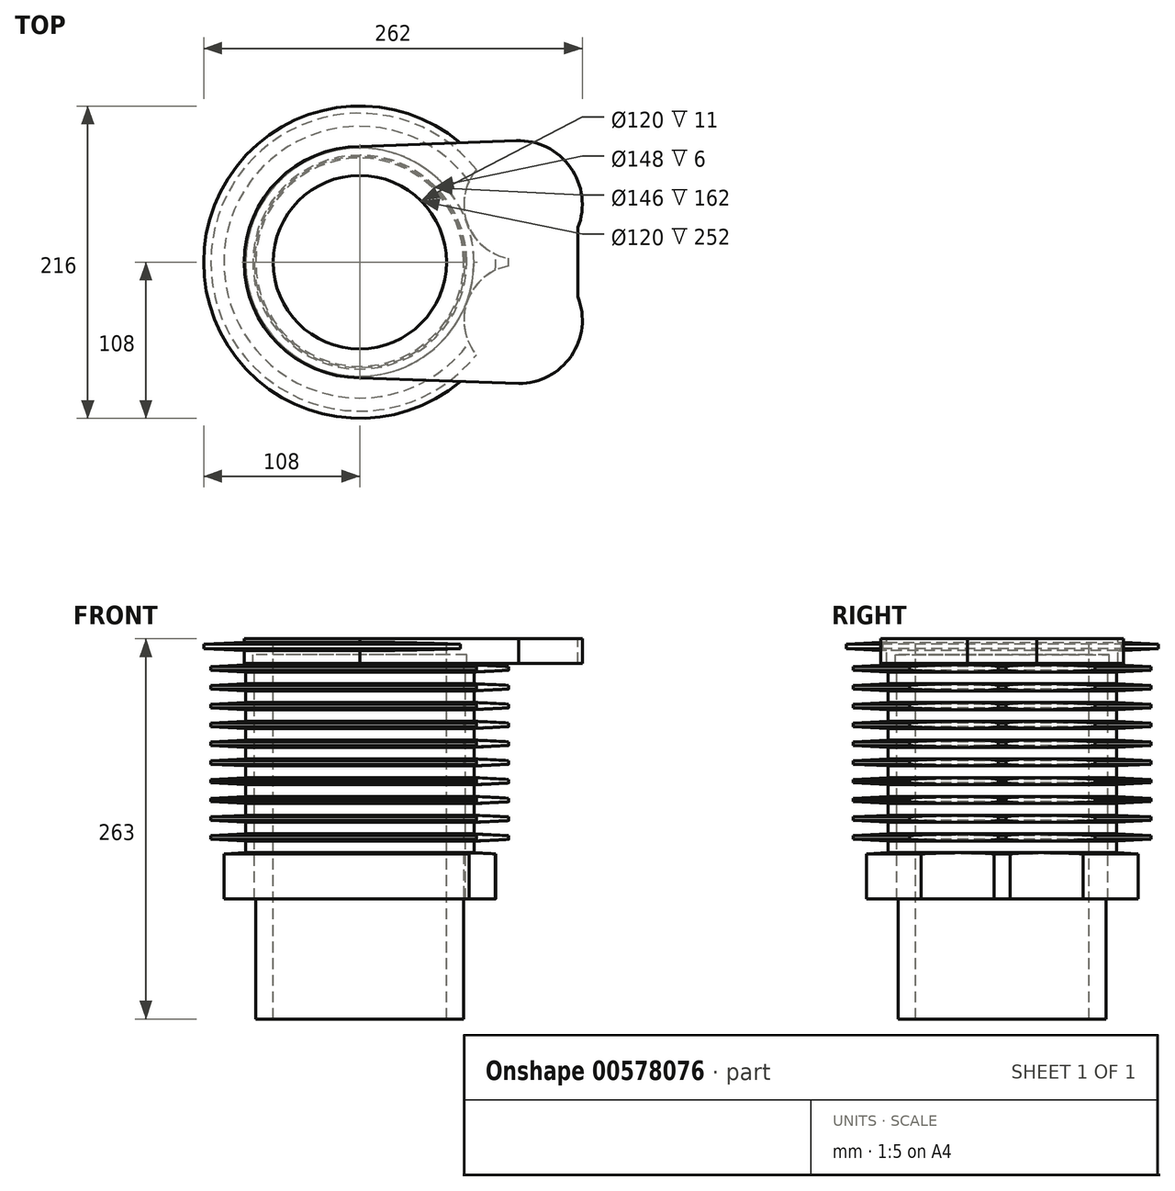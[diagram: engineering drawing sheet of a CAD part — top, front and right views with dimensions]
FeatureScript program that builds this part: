
annotation { "Feature Type Name" : "Feature", "Feature Type Description" : "" }
export const myFeature = defineFeature(function(context is Context, id is Id, definition is map)
    precondition{}
    {
        {
            var Q0;
            Q0=qCreatedBy(makeId("Front.planeOp"),FACE);
            var sketch = newSketch(context, id + "F0", { "sketchPlane" : qUnion([Q0])});
            skLineSegment(sketch, "E0", {"start": v(-60, 0) * mm, "end": v(-60, -252) * mm});
            skLineSegment(sketch, "E1", {"start": v(-60, 0) * mm, "end": v(-74, 0) * mm});
            skLineSegment(sketch, "E2", {"start": v(-65, 0) * mm, "end": v(-65, -179.28) * mm});
            skLineSegment(sketch, "E3", {"start": v(-74, 0) * mm, "end": v(-74, -7) * mm});
            skLineSegment(sketch, "E4", {"start": v(-74, -7) * mm, "end": v(-73, -7) * mm});
            skLineSegment(sketch, "E5", {"start": v(-73, -7) * mm, "end": v(-73, -169) * mm});
            skLineSegment(sketch, "E6", {"start": v(-73, -169) * mm, "end": v(-72, -169) * mm});
            skLineSegment(sketch, "E7", {"start": v(-72, -169) * mm, "end": v(-72, -252) * mm});
            skLineSegment(sketch, "E8", {"start": v(-72, -252) * mm, "end": v(-60, -252) * mm});
            skLineSegment(sketch, "E9", {"start": v(0, 0) * mm, "end": v(0, -66.25) * mm});
            skSolve(sketch);
        }
        {
            var Q0;
            {var subQ3=sQuery(id+"F0.wireOp",EDGE,"E0");Q0=makeQuery(id+"F0.imprint","IMPRINT",FACE,{"disambiguationData":[TD([[makeQuery(id+"F0.imprint","IMPRINT",EDGE,{"derivedFrom":subQ3}),-1.0]])]});}
            var Q1;
            Q1=sQuery(id+"F0.wireOp",EDGE,"E9");
            revolve(context, id + "F1", {"entities" : qUnion([Q0]), "axis" : qUnion([Q1]), "revolveType" : RevolveType.FULL});
        }
        {
            var Q0;
            Q0=qCreatedBy(makeId("Front.planeOp"),FACE);
            var sketch = newSketch(context, id + "F2", { "sketchPlane" : qUnion([Q0])});
            skLineSegment(sketch, "E10.0", {"start": v(-73, -7) * mm, "end": v(-73, -169) * mm});
            skLineSegment(sketch, "E11", {"start": v(-103, -8.26) * mm, "end": v(-103, -10.76) * mm});
            skLineSegment(sketch, "E12.0", {"start": v(-79, -7) * mm, "end": v(-79, -169) * mm});
            skLineSegment(sketch, "E13", {"start": v(-73, -7) * mm, "end": v(-79, -7) * mm});
            skLineSegment(sketch, "E14", {"start": v(-79, -7) * mm, "end": v(-103, -8.26) * mm});
            skPoint(sketch, "E15.orphan", {"position": v(-103, -9.1) * mm});
            skLineSegment(sketch, "E16", {"start": v(-103, -10.76) * mm, "end": v(-79, -12.02) * mm});
            skLineSegment(sketch, "E17", {"start": v(-79, -169) * mm, "end": v(-73, -169) * mm});
            skLineSegment(sketch, "E18.0.1.0", {"start": v(-79, -20) * mm, "end": v(-103, -21.26) * mm});
            skLineSegment(sketch, "E18.0.1.1", {"start": v(-103, -23.76) * mm, "end": v(-79, -25.02) * mm});
            skLineSegment(sketch, "E18.0.1.2", {"start": v(-103, -21.26) * mm, "end": v(-103, -23.76) * mm});
            skLineSegment(sketch, "E18.0.2.0", {"start": v(-79, -33) * mm, "end": v(-103, -34.26) * mm});
            skLineSegment(sketch, "E18.0.2.1", {"start": v(-103, -36.76) * mm, "end": v(-79, -38.02) * mm});
            skLineSegment(sketch, "E18.0.2.2", {"start": v(-103, -34.26) * mm, "end": v(-103, -36.76) * mm});
            skLineSegment(sketch, "E18.0.3.0", {"start": v(-79, -46) * mm, "end": v(-103, -47.26) * mm});
            skLineSegment(sketch, "E18.0.3.1", {"start": v(-103, -49.76) * mm, "end": v(-79, -51.02) * mm});
            skLineSegment(sketch, "E18.0.3.2", {"start": v(-103, -47.26) * mm, "end": v(-103, -49.76) * mm});
            skLineSegment(sketch, "E18.0.4.0", {"start": v(-79, -59) * mm, "end": v(-103, -60.26) * mm});
            skLineSegment(sketch, "E18.0.4.1", {"start": v(-103, -62.76) * mm, "end": v(-79, -64.02) * mm});
            skLineSegment(sketch, "E18.0.4.2", {"start": v(-103, -60.26) * mm, "end": v(-103, -62.76) * mm});
            skLineSegment(sketch, "E18.0.5.0", {"start": v(-79, -72) * mm, "end": v(-103, -73.26) * mm});
            skLineSegment(sketch, "E18.0.5.1", {"start": v(-103, -75.76) * mm, "end": v(-79, -77.02) * mm});
            skLineSegment(sketch, "E18.0.5.2", {"start": v(-103, -73.26) * mm, "end": v(-103, -75.76) * mm});
            skLineSegment(sketch, "E18.0.6.0", {"start": v(-79, -85) * mm, "end": v(-103, -86.26) * mm});
            skLineSegment(sketch, "E18.0.6.1", {"start": v(-103, -88.76) * mm, "end": v(-79, -90.02) * mm});
            skLineSegment(sketch, "E18.0.6.2", {"start": v(-103, -86.26) * mm, "end": v(-103, -88.76) * mm});
            skLineSegment(sketch, "E18.0.7.0", {"start": v(-79, -98) * mm, "end": v(-103, -99.26) * mm});
            skLineSegment(sketch, "E18.0.7.1", {"start": v(-103, -101.76) * mm, "end": v(-79, -103.02) * mm});
            skLineSegment(sketch, "E18.0.7.2", {"start": v(-103, -99.26) * mm, "end": v(-103, -101.76) * mm});
            skLineSegment(sketch, "E18.0.8.0", {"start": v(-79, -111) * mm, "end": v(-103, -112.26) * mm});
            skLineSegment(sketch, "E18.0.8.1", {"start": v(-103, -114.76) * mm, "end": v(-79, -116.02) * mm});
            skLineSegment(sketch, "E18.0.8.2", {"start": v(-103, -112.26) * mm, "end": v(-103, -114.76) * mm});
            skLineSegment(sketch, "E18.0.9.0", {"start": v(-79, -124) * mm, "end": v(-103, -125.26) * mm});
            skLineSegment(sketch, "E18.0.9.1", {"start": v(-103, -127.76) * mm, "end": v(-79, -129.02) * mm});
            skLineSegment(sketch, "E18.0.9.2", {"start": v(-103, -125.26) * mm, "end": v(-103, -127.76) * mm});
            skLineSegment(sketch, "E18.direction1", {"start": v(-79, -7) * mm, "end": v(-54, -7) * mm, "construction": true});
            skLineSegment(sketch, "E18.direction2", {"start": v(-79, -7) * mm, "end": v(-79, -20) * mm, "construction": true});
            skLineSegment(sketch, "E19", {"start": v(-79, -169) * mm, "end": v(-94, -169) * mm});
            skLineSegment(sketch, "E20", {"start": v(-94, -169) * mm, "end": v(-94, -137.79) * mm});
            skLineSegment(sketch, "E21", {"start": v(-94, -139.02) * mm, "end": v(-79, -139.02) * mm});
            skLineSegment(sketch, "E22.0", {"start": v(0, 0) * mm, "end": v(0, -66.25) * mm});
            skLineSegment(sketch, "E23.0.0.10", {"start": v(-79, -137) * mm, "end": v(-103, -138.26) * mm});
            skLineSegment(sketch, "E23.3.0.10", {"start": v(-103, -140.76) * mm, "end": v(-79, -142.02) * mm});
            skLineSegment(sketch, "E23.6.0.10", {"start": v(-103, -138.26) * mm, "end": v(-103, -140.76) * mm});
            skSolve(sketch);
        }
        {
            var Q0;
            {var subQ0=sQuery(id+"F2.wireOp",EDGE,"E19");Q0=makeQuery(id+"F2.imprint","IMPRINT",FACE,{"disambiguationData":[TD([[makeQuery(id+"F2.imprint","IMPRINT",EDGE,{"derivedFrom":subQ0}),-1.0]])]});}
            var Q1;
            Q1=makeQuery(id+"F2.imprint","IMPRINT",FACE,{"disambiguationData":[TD([[makeQuery(id+"F2.imprint","IMPRINT",EDGE,{"derivedFrom":sQuery(id+"F2.wireOp",EDGE,"E10.0")}),-1.0]])]});
            var Q2;
            {var subQ0=sQuery(id+"F2.wireOp",EDGE,"E18.0.9.0");Q2=makeQuery(id+"F2.imprint","IMPRINT",FACE,{"disambiguationData":[TD([[makeQuery(id+"F2.imprint","IMPRINT",EDGE,{"derivedFrom":subQ0}),1.0]])]});}
            var Q3;
            {var subQ0=sQuery(id+"F2.wireOp",EDGE,"E18.0.8.0");Q3=makeQuery(id+"F2.imprint","IMPRINT",FACE,{"disambiguationData":[TD([[makeQuery(id+"F2.imprint","IMPRINT",EDGE,{"derivedFrom":subQ0}),1.0]])]});}
            var Q4;
            {var subQ0=sQuery(id+"F2.wireOp",EDGE,"E18.0.7.0");Q4=makeQuery(id+"F2.imprint","IMPRINT",FACE,{"disambiguationData":[TD([[makeQuery(id+"F2.imprint","IMPRINT",EDGE,{"derivedFrom":subQ0}),1.0]])]});}
            var Q5;
            {var subQ0=sQuery(id+"F2.wireOp",EDGE,"E18.0.6.0");Q5=makeQuery(id+"F2.imprint","IMPRINT",FACE,{"disambiguationData":[TD([[makeQuery(id+"F2.imprint","IMPRINT",EDGE,{"derivedFrom":subQ0}),1.0]])]});}
            var Q6;
            {var subQ0=sQuery(id+"F2.wireOp",EDGE,"E18.0.5.0");Q6=makeQuery(id+"F2.imprint","IMPRINT",FACE,{"disambiguationData":[TD([[makeQuery(id+"F2.imprint","IMPRINT",EDGE,{"derivedFrom":subQ0}),1.0]])]});}
            var Q7;
            {var subQ0=sQuery(id+"F2.wireOp",EDGE,"E18.0.4.0");Q7=makeQuery(id+"F2.imprint","IMPRINT",FACE,{"disambiguationData":[TD([[makeQuery(id+"F2.imprint","IMPRINT",EDGE,{"derivedFrom":subQ0}),1.0]])]});}
            var Q8;
            {var subQ0=sQuery(id+"F2.wireOp",EDGE,"E18.0.3.0");Q8=makeQuery(id+"F2.imprint","IMPRINT",FACE,{"disambiguationData":[TD([[makeQuery(id+"F2.imprint","IMPRINT",EDGE,{"derivedFrom":subQ0}),1.0]])]});}
            var Q9;
            {var subQ0=sQuery(id+"F2.wireOp",EDGE,"E18.0.2.0");Q9=makeQuery(id+"F2.imprint","IMPRINT",FACE,{"disambiguationData":[TD([[makeQuery(id+"F2.imprint","IMPRINT",EDGE,{"derivedFrom":subQ0}),1.0]])]});}
            var Q10;
            {var subQ0=sQuery(id+"F2.wireOp",EDGE,"E18.0.1.0");Q10=makeQuery(id+"F2.imprint","IMPRINT",FACE,{"disambiguationData":[TD([[makeQuery(id+"F2.imprint","IMPRINT",EDGE,{"derivedFrom":subQ0}),1.0]])]});}
            var Q11;
            Q11=makeQuery(id+"F2.imprint","IMPRINT",FACE,{"disambiguationData":[TD([[makeQuery(id+"F2.imprint","IMPRINT",EDGE,{"derivedFrom":sQuery(id+"F2.wireOp",EDGE,"E11")}),1.0]])]});
            var Q12;
            {var subQ0=sQuery(id+"F2.wireOp",EDGE,"E21");Q12=makeQuery(id+"F2.imprint","IMPRINT",FACE,{"disambiguationData":[TD([[makeQuery(id+"F2.imprint","IMPRINT",EDGE,{"derivedFrom":subQ0}),1.0]])]});}
            var Q13;
            {var subQ0=sQuery(id+"F2.wireOp",EDGE,"E21");Q13=makeQuery(id+"F2.imprint","IMPRINT",FACE,{"disambiguationData":[TD([[makeQuery(id+"F2.imprint","IMPRINT",EDGE,{"derivedFrom":subQ0}),-1.0]])]});}
            var Q14;
            Q14=sQuery(id+"F0.wireOp",EDGE,"E9");
            revolve(context, id + "F3", {"entities" : qUnion([Q0, Q1, Q2, Q3, Q4, Q5, Q6, Q7, Q8, Q9, Q10, Q11, Q12, Q13]), "axis" : qUnion([Q14]), "revolveType" : RevolveType.FULL});
        }
        {
            var Q0;
            Q0=makeQuery(id+"F3.opRevolve","SWEPT_FACE",FACE,{"disambiguationData":[OSD([sQuery(id+"F2.wireOp",EDGE,"E17"),sQuery(id+"F2.wireOp",EDGE,"E19")])]});
            var sketch = newSketch(context, id + "F4", { "sketchPlane" : qUnion([Q0])});
            skCircle(sketch, "E24", {"center": v(110, 40) * mm, "radius": 38 * mm});
            skCircle(sketch, "E25", {"center": v(110, -40) * mm, "radius": 38 * mm});
            skSolve(sketch);
        }
        {
            var Q0;
            {var subQ0=sQuery(id+"F4.wireOp",EDGE,"E24");var subQ1=makeQuery(id+"F3.opRevolve","SWEPT_EDGE",EDGE,{"disambiguationData":[OSD([sQuery(id+"F2.wireOp",EDGE,"E19"),sQuery(id+"F2.wireOp",EDGE,"E20")])]});var subQ2=makeQuery(id+"F4.imprint","INTERSECT",VERTEX,{"disambiguationData":[OD(0.0)],"derivedFrom":[subQ1,subQ0]});Q0=makeQuery(id+"F4.imprint","IMPRINT",FACE,{"disambiguationData":[TD([[makeQuery(id+"F4.imprint","IMPRINT",EDGE,{"disambiguationData":[TD([[subQ2,-1.0]])],"derivedFrom":subQ0}),1.0]])]});}
            var Q1;
            {var subQ0=sQuery(id+"F4.wireOp",EDGE,"E25");var subQ1=makeQuery(id+"F3.opRevolve","SWEPT_EDGE",EDGE,{"disambiguationData":[OSD([sQuery(id+"F2.wireOp",EDGE,"E19"),sQuery(id+"F2.wireOp",EDGE,"E20")])]});var subQ2=makeQuery(id+"F4.imprint","INTERSECT",VERTEX,{"disambiguationData":[OD(0.0)],"derivedFrom":[subQ1,subQ0]});Q1=makeQuery(id+"F4.imprint","IMPRINT",FACE,{"disambiguationData":[TD([[makeQuery(id+"F4.imprint","IMPRINT",EDGE,{"disambiguationData":[TD([[subQ2,-1.0]])],"derivedFrom":subQ0}),1.0]])]});}
            var Q2;
            {var subQ0=sQuery(id+"F4.wireOp",EDGE,"E24");var subQ1=makeQuery(id+"F3.opRevolve","SWEPT_EDGE",EDGE,{"disambiguationData":[OSD([sQuery(id+"F2.wireOp",EDGE,"E19"),sQuery(id+"F2.wireOp",EDGE,"E20")])]});var subQ2=makeQuery(id+"F4.imprint","INTERSECT",VERTEX,{"disambiguationData":[OD(0.0)],"derivedFrom":[subQ1,subQ0]});Q2=makeQuery(id+"F4.imprint","IMPRINT",FACE,{"disambiguationData":[TD([[makeQuery(id+"F4.imprint","IMPRINT",EDGE,{"disambiguationData":[TD([[subQ2,1.0]])],"derivedFrom":subQ0}),1.0]])]});}
            var Q3;
            {var subQ0=sQuery(id+"F4.wireOp",EDGE,"E25");var subQ1=makeQuery(id+"F3.opRevolve","SWEPT_EDGE",EDGE,{"disambiguationData":[OSD([sQuery(id+"F2.wireOp",EDGE,"E19"),sQuery(id+"F2.wireOp",EDGE,"E20")])]});var subQ2=makeQuery(id+"F4.imprint","INTERSECT",VERTEX,{"disambiguationData":[OD(0.0)],"derivedFrom":[subQ1,subQ0]});Q3=makeQuery(id+"F4.imprint","IMPRINT",FACE,{"disambiguationData":[TD([[makeQuery(id+"F4.imprint","IMPRINT",EDGE,{"disambiguationData":[TD([[subQ2,1.0]])],"derivedFrom":subQ0}),1.0]])]});}
            extrude(context, id + "F5", {"entities" : qUnion([Q0, Q1, Q2, Q3]), "operationType" : NewBodyOperationType.REMOVE, "oppositeDirection" : true, "depth" : 200 * mm, "offsetDistance" : 25 * mm});
        }
        {
            var Q0;
            Q0=qCreatedBy(makeId("Front.planeOp"),FACE);
            var sketch = newSketch(context, id + "F6", { "sketchPlane" : qUnion([Q0])});
            skLineSegment(sketch, "E26.0", {"start": v(-60, 0) * mm, "end": v(-74, 0) * mm});
            skLineSegment(sketch, "E27", {"start": v(-74, 0) * mm, "end": v(-74, -6) * mm});
            skLineSegment(sketch, "E28", {"start": v(-74, -6) * mm, "end": v(-80, -6) * mm});
            skLineSegment(sketch, "E29", {"start": v(-80, -6) * mm, "end": v(-80, 4) * mm});
            skLineSegment(sketch, "E30", {"start": v(-80, 4) * mm, "end": v(-60, 4) * mm});
            skLineSegment(sketch, "E31", {"start": v(-60, 4) * mm, "end": v(-60, 0) * mm});
            skLineSegment(sketch, "E32.0", {"start": v(0, 0) * mm, "end": v(0, -66.25) * mm});
            skSolve(sketch);
        }
        {
            var Q0;
            Q0=makeQuery(id+"F6.imprint","IMPRINT",FACE,{"disambiguationData":[TD([[makeQuery(id+"F6.imprint","IMPRINT",EDGE,{"derivedFrom":sQuery(id+"F6.wireOp",EDGE,"E26.0")}),-1.0]])]});
            var Q1;
            Q1=sQuery(id+"F6.wireOp",EDGE,"E32.0");
            revolve(context, id + "F7", {"entities" : qUnion([Q0]), "axis" : qUnion([Q1]), "revolveType" : RevolveType.FULL});
        }
        {
            var Q0;
            Q0=makeQuery(id+"F7.opRevolve","SWEPT_FACE",FACE,{"disambiguationData":[OSD([sQuery(id+"F6.wireOp",EDGE,"E30")])]});
            var sketch = newSketch(context, id + "F8", { "sketchPlane" : qUnion([Q0])});
            skLineSegment(sketch, "E33", {"start": v(151, -55.97) * mm, "end": v(151, 55.97) * mm});
            skCircle(sketch, "E34", {"center": v(110, 40) * mm, "radius": 44 * mm});
            skCircle(sketch, "E35", {"center": v(110, -40) * mm, "radius": 44 * mm});
            skPoint(sketch, "E36.orphan", {"position": v(151, 80) * mm});
            skPoint(sketch, "E37.orphan", {"position": v(0, 80) * mm});
            skPoint(sketch, "E38.orphan", {"position": v(151, -80) * mm});
            skPoint(sketch, "E39.start.orphan", {"position": v(0, -80) * mm});
            skLineSegment(sketch, "E40", {"start": v(0, 80) * mm, "end": v(110, 84.03) * mm});
            skLineSegment(sketch, "E41", {"start": v(0, -80) * mm, "end": v(110, -84) * mm});
            skSolve(sketch);
        }
        {
            var Q0;
            {var subQ0=sQuery(id+"F8.wireOp",EDGE,"E40");var subQ1=sQuery(id+"F8.wireOp",EDGE,"E34");var subQ2=makeQuery(id+"F8.imprint","INTERSECT",VERTEX,{"derivedFrom":[subQ1,subQ0]});Q0=makeQuery(id+"F8.imprint","IMPRINT",FACE,{"disambiguationData":[TD([[makeQuery(id+"F8.imprint","IMPRINT",EDGE,{"disambiguationData":[TD([[subQ2,-1.0]])],"derivedFrom":subQ1}),-1.0]])]});}
            var Q1;
            {var subQ1=sQuery(id+"F8.wireOp",EDGE,"E34");var subQ7=sQuery(id+"F8.wireOp",EDGE,"E33");var subQ8=makeQuery(id+"F8.imprint","INTERSECT",VERTEX,{"disambiguationData":[OD(0.0)],"derivedFrom":[subQ7,subQ1]});Q1=makeQuery(id+"F8.imprint","IMPRINT",FACE,{"disambiguationData":[TD([[makeQuery(id+"F8.imprint","IMPRINT",EDGE,{"disambiguationData":[TD([[subQ8,1.0]])],"derivedFrom":subQ7}),1.0]])]});}
            var Q2;
            {var subQ0=sQuery(id+"F8.wireOp",EDGE,"E35");var subQ1=sQuery(id+"F8.wireOp",EDGE,"E33");var subQ2=makeQuery(id+"F8.imprint","INTERSECT",VERTEX,{"disambiguationData":[OD(1.0)],"derivedFrom":[subQ1,subQ0]});Q2=makeQuery(id+"F8.imprint","IMPRINT",FACE,{"disambiguationData":[TD([[makeQuery(id+"F8.imprint","IMPRINT",EDGE,{"disambiguationData":[TD([[subQ2,-1.0]])],"derivedFrom":subQ1}),1.0]])]});}
            var Q3;
            {var subQ0=sQuery(id+"F8.wireOp",EDGE,"E35");var subQ1=sQuery(id+"F8.wireOp",EDGE,"E34");var subQ2=makeQuery(id+"F8.imprint","INTERSECT",VERTEX,{"disambiguationData":[OD(0.0)],"derivedFrom":[subQ1,subQ0]});Q3=makeQuery(id+"F8.imprint","IMPRINT",FACE,{"disambiguationData":[TD([[makeQuery(id+"F8.imprint","IMPRINT",EDGE,{"disambiguationData":[TD([[subQ2,1.0]])],"derivedFrom":subQ1}),-1.0]])]});}
            var Q4;
            {var subQ0=sQuery(id+"F8.wireOp",EDGE,"E35");var subQ6=sQuery(id+"F8.wireOp",EDGE,"E33");var subQ8=makeQuery(id+"F8.imprint","INTERSECT",VERTEX,{"disambiguationData":[OD(0.0)],"derivedFrom":[subQ6,subQ0]});Q4=makeQuery(id+"F8.imprint","IMPRINT",FACE,{"disambiguationData":[TD([[makeQuery(id+"F8.imprint","IMPRINT",EDGE,{"disambiguationData":[TD([[subQ8,-1.0]])],"derivedFrom":subQ6}),1.0]])]});}
            var Q5;
            {var subQ0=sQuery(id+"F8.wireOp",EDGE,"E35");var subQ1=sQuery(id+"F8.wireOp",EDGE,"E34");var subQ2=makeQuery(id+"F8.imprint","INTERSECT",VERTEX,{"disambiguationData":[OD(0.0)],"derivedFrom":[subQ1,subQ0]});Q5=makeQuery(id+"F8.imprint","IMPRINT",FACE,{"disambiguationData":[TD([[makeQuery(id+"F8.imprint","IMPRINT",EDGE,{"disambiguationData":[TD([[subQ2,-1.0]])],"derivedFrom":subQ1}),1.0]])]});}
            var Q6;
            {var subQ0=sQuery(id+"F8.wireOp",EDGE,"E35");var subQ1=sQuery(id+"F8.wireOp",EDGE,"E33");var subQ2=makeQuery(id+"F8.imprint","INTERSECT",VERTEX,{"disambiguationData":[OD(0.0)],"derivedFrom":[subQ1,subQ0]});Q6=makeQuery(id+"F8.imprint","IMPRINT",FACE,{"disambiguationData":[TD([[makeQuery(id+"F8.imprint","IMPRINT",EDGE,{"disambiguationData":[TD([[subQ2,-1.0]])],"derivedFrom":subQ1}),-1.0]])]});}
            var Q7;
            {var subQ0=sQuery(id+"F8.wireOp",EDGE,"E34");var subQ1=sQuery(id+"F8.wireOp",EDGE,"E33");var subQ2=makeQuery(id+"F8.imprint","INTERSECT",VERTEX,{"disambiguationData":[OD(0.0)],"derivedFrom":[subQ1,subQ0]});Q7=makeQuery(id+"F8.imprint","IMPRINT",FACE,{"disambiguationData":[TD([[makeQuery(id+"F8.imprint","IMPRINT",EDGE,{"disambiguationData":[TD([[subQ2,1.0]])],"derivedFrom":subQ1}),-1.0]])]});}
            var Q8;
            {var subQ0=sQuery(id+"F8.wireOp",EDGE,"E41");var subQ1=sQuery(id+"F8.wireOp",EDGE,"E35");var subQ2=makeQuery(id+"F8.imprint","INTERSECT",VERTEX,{"disambiguationData":[OD(1.0)],"derivedFrom":[subQ1,subQ0]});Q8=makeQuery(id+"F8.imprint","IMPRINT",FACE,{"disambiguationData":[TD([[makeQuery(id+"F8.imprint","IMPRINT",EDGE,{"disambiguationData":[TD([[subQ2,1.0]])],"derivedFrom":subQ1}),-1.0]])]});}
            extrude(context, id + "F9", {"entities" : qUnion([Q0, Q1, Q2, Q3, Q4, Q5, Q6, Q7, Q8]), "operationType" : NewBodyOperationType.ADD, "oppositeDirection" : true, "depth" : 10 * mm, "offsetDistance" : 25 * mm});
        }
        {
            var Q0;
            {var subQ0=sQuery(id+"F6.wireOp",EDGE,"E30");Q0=makeQuery(id+"F9.boolean.opBoolean","MERGE",FACE,{"derivedFrom":[makeQuery(id+"F7.opRevolve","SWEPT_FACE",FACE,{"disambiguationData":[OSD([subQ0])]}),makeQuery(id+"F9.opExtrude","CAP_FACE",FACE,{"disambiguationData":[OSD([sQuery(id+"F6.wireOp",EDGE,"E29"),subQ0,sQuery(id+"F8.wireOp",EDGE,"E33"),sQuery(id+"F8.wireOp",EDGE,"E34"),sQuery(id+"F8.wireOp",EDGE,"E35"),sQuery(id+"F8.wireOp",EDGE,"E40"),sQuery(id+"F8.wireOp",EDGE,"E41")])],"isStart":true})]});}
            extrude(context, id + "F10", {"entities" : qUnion([Q0]), "operationType" : NewBodyOperationType.ADD, "depth" : 7 * mm, "offsetDistance" : 25 * mm});
        }
        {
            var Q0;
            Q0=qCreatedBy(makeId("Front.planeOp"),FACE);
            var sketch = newSketch(context, id + "F11", { "sketchPlane" : qUnion([Q0])});
            skLineSegment(sketch, "E42", {"start": v(-108, 4.18) * mm, "end": v(-108, 7.18) * mm});
            skLineSegment(sketch, "E43", {"start": v(-108, 4.18) * mm, "end": v(-73.3, 2.36) * mm});
            skLineSegment(sketch, "E44", {"start": v(-108, 7.18) * mm, "end": v(-73.3, 9) * mm});
            skLineSegment(sketch, "E45", {"start": v(-73.3, 9) * mm, "end": v(-73.3, 2.36) * mm});
            skSolve(sketch);
        }
        {
            var Q0;
            Q0=makeQuery(id+"F11.imprint","IMPRINT",FACE,{"disambiguationData":[TD([[makeQuery(id+"F11.imprint","IMPRINT",EDGE,{"derivedFrom":sQuery(id+"F11.wireOp",EDGE,"E42")}),-1.0]])]});
            var Q1;
            Q1=sQuery(id+"F0.wireOp",EDGE,"E9");
            revolve(context, id + "F12", {"operationType" : NewBodyOperationType.ADD, "entities" : qUnion([Q0]), "axis" : qUnion([Q1]), "revolveType" : RevolveType.FULL});
        }
        {
            var Q0;
            Q0=qCreatedBy(makeId("Top.planeOp"),FACE);
            cPlane(context, id + "F13", {"entities" : qUnion([Q0]), "cplaneType" : CPlaneType.OFFSET, "offset" : 25 * mm, "width" : 150 * mm, "height" : 150 * mm});
        }
    });
